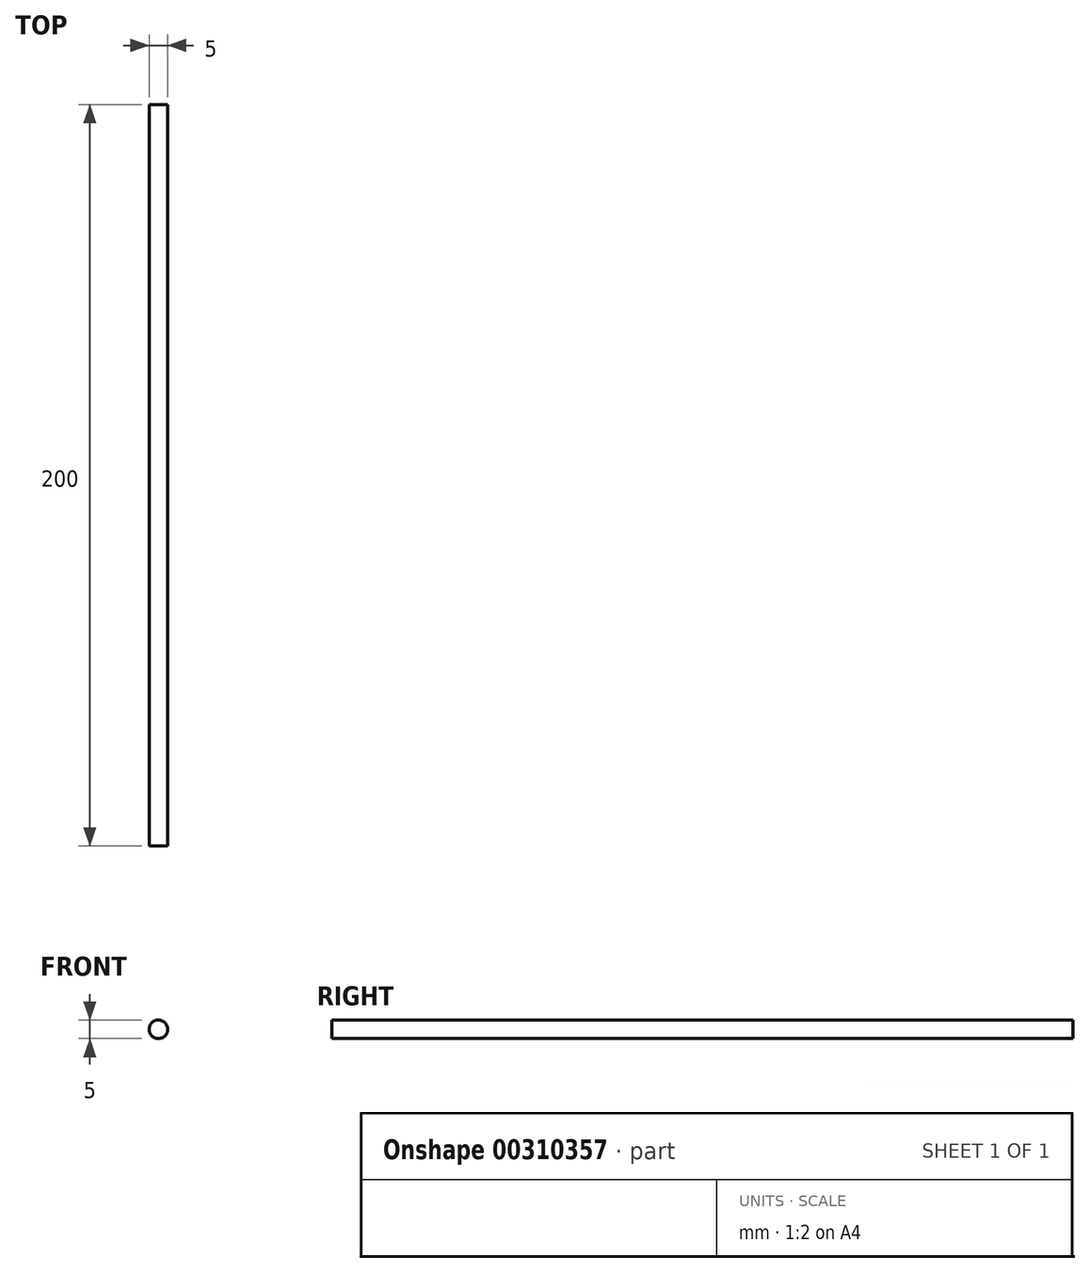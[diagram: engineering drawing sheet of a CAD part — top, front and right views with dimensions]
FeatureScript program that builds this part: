
annotation { "Feature Type Name" : "Feature", "Feature Type Description" : "" }
export const myFeature = defineFeature(function(context is Context, id is Id, definition is map)
    precondition{}
    {
        {
            var Q0;
            Q0=qCreatedBy(makeId("Front.planeOp"),FACE);
            var sketch = newSketch(context, id + "F0", { "sketchPlane" : qUnion([Q0])});
            skCircle(sketch, "E0", {"center": v(0, 0) * mm, "radius": 2.5 * mm});
            skSolve(sketch);
        }
        {
            var Q0;
            Q0 = qSketchRegion(id + "F0", true);
            extrude(context, id + "F1", {"entities" : qUnion([Q0]), "depth" : 200 * mm});
        }
    });
